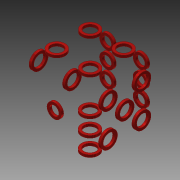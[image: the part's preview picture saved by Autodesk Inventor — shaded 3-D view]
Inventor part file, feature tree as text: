
AUTODESK INVENTOR PART (.ipt)
format: ipt  version: 2013 (Build 170138000, 138)  size: 419,840 bytes
history: native  units: mm
features: extrude x21, sketch x21, projected_geometry x19, fillet x1, plane x1, mirror x1
ambient origin geometry x8: Origin, YZ Plane, XZ Plane, XY Plane, X Axis, Y Axis, Z Axis, Center Point
bodies: Solid1 (feature_tree)
feature tree (64):
  extrude  "Extrusion1"  Depth=30.0mm
  fillet  "Fillet1"  Radius=30.0mm
  extrude  "Extrusion2"  Depth=6.0mm
  extrude  "Extrusion3"  Depth=6.0mm
  plane  "Work Plane1"
  mirror  "Mirror1"
  extrude  "Extrusion4"  Depth=6.0mm
  extrude  "Extrusion5"  Depth=7.0mm
  extrude  "Extrusion6"  Depth=7.0mm
  extrude  "Extrusion7"  Depth=1.0mm TaperAngle=0.0deg
  sketch  "Sketch8"  dims[d22=7.0mm d23=7.0mm]
  sketch  "Sketch9"  dims[d24=7.0mm d25=7.0mm]
  sketch  "Sketch10"  dims[d26=1.0mm d27=0.0mm d28=14.0mm]
  sketch  "Sketch11"  dims[d29=14.0mm d30=14.0mm]
  sketch  "Sketch12"  dims[d32=14.0mm d33=4.0mm]
  sketch  "Sketch13"  dims[d34=4.0mm d35=7.0mm]
  extrude  "Extrusion8"  Depth=7.0mm
  extrude  "Extrusion9"  Depth=7.0mm
  extrude  "Extrusion10"  Depth=14.0mm
  extrude  "Extrusion11"  Depth=14.0mm
  extrude  "Extrusion12"  Depth=4.0mm
  extrude  "Extrusion13"  Depth=7.0mm
  extrude  "Extrusion14"  Depth=1.0mm TaperAngle=0.0deg
  sketch  "Sketch16"  dims[d39=7.0mm d40=14.0mm]
  sketch  "Sketch17"  dims[d42=14.0mm d43=4.0mm]
  sketch  "Sketch18"  dims[d44=4.0mm d45=7.0mm]
  sketch  "Sketch19"  dims[d46=7.0mm d47=1.0mm d48=0.0mm]
  sketch  "Sketch20"  dims[d49=14.0mm d51=14.0mm]
  sketch  "Sketch21"  dims[d52=4.0mm d53=4.0mm]
  extrude  "Extrusion16"  Depth=14.0mm
  extrude  "Extrusion17"  Depth=4.0mm
  extrude  "Extrusion18"  Depth=7.0mm
  extrude  "Extrusion19"  Depth=1.0mm TaperAngle=0.0deg
  extrude  "Extrusion20"  Depth=14.0mm
  extrude  "Extrusion21"  Depth=4.0mm
  extrude  "Extrusion22"  Depth=7.0mm
  sketch  "Sketch1"  dims[d0=30.0mm d2=30.0mm d3=30.0mm d4=0.0mm]
  sketch  "Sketch2"  dims[d5=4.0mm d6=6.0mm]
  sketch  "Sketch3"  dims[d9=1.0mm d10=0.0mm d11=6.0mm]
  sketch  "Sketch4"  dims[d13=6.0mm d14=6.0mm]
  sketch  "Sketch5"  dims[d15=7.0mm d16=7.0mm]
  sketch  "Sketch6"  dims[d17=0.0mm d18=7.0mm]
  sketch  "Sketch7"  dims[d19=0.0mm d20=1.0mm d21=0.0mm]
  sketch  "Sketch15"  dims[d36=7.0mm d37=1.0mm d38=0.0mm]
  projected_geometry  "Projected Loop1"
  projected_geometry  "Projected Loop2"
  projected_geometry  "Projected Loop3"
  projected_geometry  "Projected Loop4"
  projected_geometry  "Projected Loop5"
  projected_geometry  "Projected Loop6"
  projected_geometry  "Projected Loop7"
  projected_geometry  "Projected Loop8"
  projected_geometry  "Projected Loop9"
  projected_geometry  "Projected Loop10"
  projected_geometry  "Projected Loop11"
  projected_geometry  "Projected Loop12"
  projected_geometry  "Projected Loop13"
  projected_geometry  "Projected Loop14"
  projected_geometry  "Projected Loop15"
  projected_geometry  "Projected Loop16"
  projected_geometry  "Projected Loop17"
  projected_geometry  "Projected Loop18"
  projected_geometry  "Projected Loop19"
  sketch  "Sketch23"  dims[d54=7.0mm d55=7.0mm d56=7.0mm d57=7.0mm d58=7.0mm d59=1.0mm d60=0.0mm d61=0.0mm d62=0.0mm d63=1.0mm d64=1.0mm d65=1.0mm d66=1.0mm d67=1.0mm d68=1.0mm d69=1.0mm d70=1.0mm d71=1.0mm d72=1.0mm d73=1.0mm d74=1.0mm d75=1.0mm d76=5.0mm d77=1.0mm d78=1.0mm d79=1.0mm d80=1.0mm d81=1.0mm d82=1.0mm d85=1.0mm d86=1.0mm d87=0.0mm d88=1.0mm d89=0.0mm d90=1.0mm d91=0.0mm d92=1.0mm d93=0.0mm d94=1.0mm d95=0.0mm d96=1.0mm d97=0.0mm d100=100.0mm d101=0.0mm d102=1.0mm d103=0.0mm d104=1.0mm d105=0.0mm d106=1.0mm d107=0.0mm d108=1.0mm d109=0.0mm d110=1.0mm d111=0.0mm d112=1.0mm d113=0.0mm]
